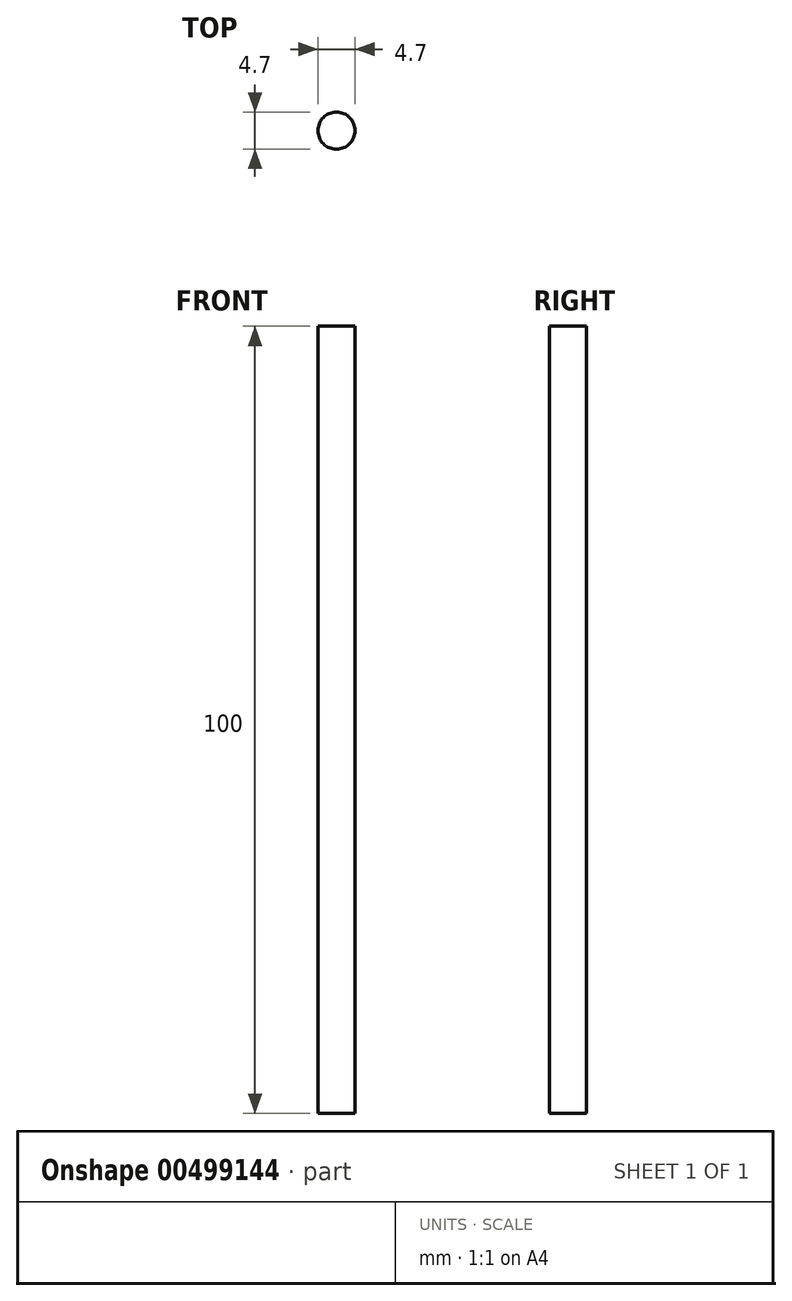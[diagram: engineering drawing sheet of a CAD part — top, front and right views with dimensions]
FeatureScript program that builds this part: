
annotation { "Feature Type Name" : "Feature", "Feature Type Description" : "" }
export const myFeature = defineFeature(function(context is Context, id is Id, definition is map)
    precondition{}
    {
        {
            var Q0;
            Q0=qCreatedBy(makeId("Top.planeOp"),FACE);
            var sketch = newSketch(context, id + "F0", { "sketchPlane" : qUnion([Q0])});
            skCircle(sketch, "E0", {"center": v(0, 0) * mm, "radius": 2.35 * mm});
            skSolve(sketch);
        }
        {
            var Q0;
            Q0=makeQuery(id+"F0.imprint","IMPRINT",FACE,{"disambiguationData":[TD([[makeQuery(id+"F0.imprint","IMPRINT",EDGE,{"derivedFrom":sQuery(id+"F0.wireOp",EDGE,"E0")}),1.0]])]});
            extrude(context, id + "F1", {"entities" : qUnion([Q0]), "depth" : 100 * mm});
        }
    });
